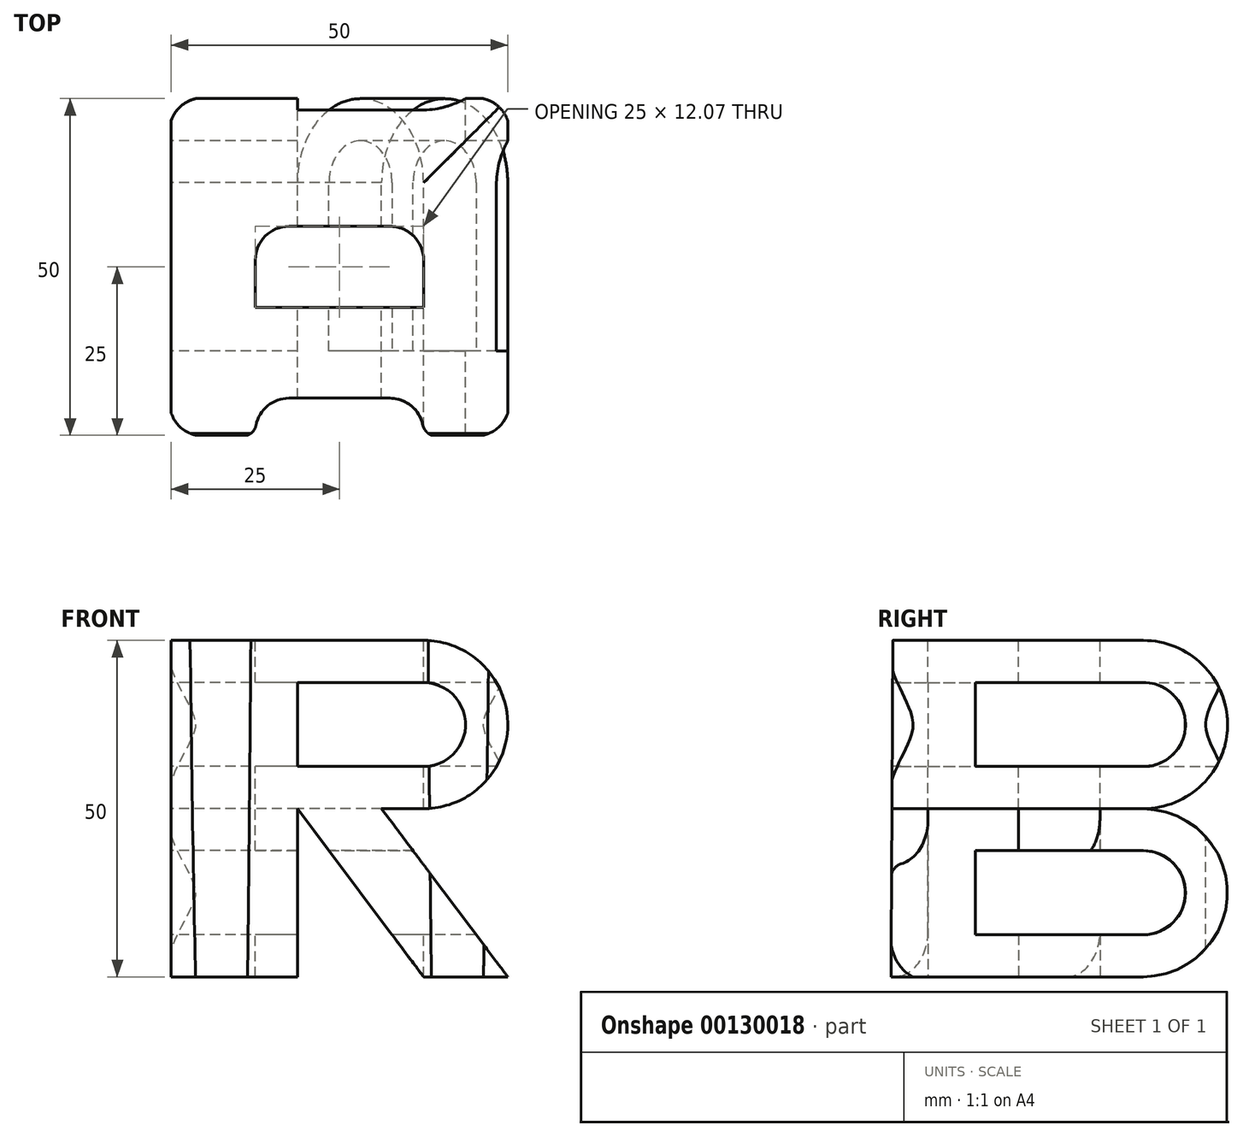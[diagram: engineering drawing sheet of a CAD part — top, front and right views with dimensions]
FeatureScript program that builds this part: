
annotation { "Feature Type Name" : "Feature", "Feature Type Description" : "" }
export const myFeature = defineFeature(function(context is Context, id is Id, definition is map)
    precondition{}
    {
        {
            var Q0;
            Q0=qCreatedBy(makeId("Front.planeOp"),FACE);
            var sketch = newSketch(context, id + "F0", { "sketchPlane" : qUnion([Q0])});
            skLineSegment(sketch, "E0.bottom", {"start": v(25, 25) * mm, "end": v(-25, 25) * mm, "construction": true});
            skLineSegment(sketch, "E0.top", {"start": v(25, -25) * mm, "end": v(-25, -25) * mm, "construction": true});
            skLineSegment(sketch, "E0.left", {"start": v(25, 25) * mm, "end": v(25, -25) * mm, "construction": true});
            skLineSegment(sketch, "E0.right", {"start": v(-25, 25) * mm, "end": v(-25, -25) * mm, "construction": true});
            skPoint(sketch, "E0.middle", {"position": v(0, 0) * mm});
            skLineSegment(sketch, "E1", {"start": v(0, 25) * mm, "end": v(0, -25) * mm, "construction": true});
            skLineSegment(sketch, "E2", {"start": v(25, 0) * mm, "end": v(-25, 0) * mm, "construction": true});
            skLineSegment(sketch, "E3", {"start": v(-25, 18.75) * mm, "end": v(25, 18.75) * mm, "construction": true});
            skLineSegment(sketch, "E4", {"start": v(-25, 12.5) * mm, "end": v(25, 12.5) * mm, "construction": true});
            skLineSegment(sketch, "E5", {"start": v(25, 12.5) * mm, "end": v(24.97, 10.97) * mm, "construction": true});
            skLineSegment(sketch, "E6", {"start": v(-25.04, 6.25) * mm, "end": v(25, 6.25) * mm, "construction": true});
            skLineSegment(sketch, "E7", {"start": v(-25, -6.25) * mm, "end": v(25, -6.25) * mm, "construction": true});
            skLineSegment(sketch, "E8", {"start": v(-25, -12.5) * mm, "end": v(25, -12.5) * mm, "construction": true});
            skLineSegment(sketch, "E9", {"start": v(-25, -18.75) * mm, "end": v(25, -18.75) * mm, "construction": true});
            skLineSegment(sketch, "E10", {"start": v(18.75, -25) * mm, "end": v(18.75, 25) * mm, "construction": true});
            skLineSegment(sketch, "E11", {"start": v(6.25, 25) * mm, "end": v(6.25, -25) * mm, "construction": true});
            skLineSegment(sketch, "E12", {"start": v(12.5, -25) * mm, "end": v(12.5, 25) * mm, "construction": true});
            skLineSegment(sketch, "E13", {"start": v(-6.25, 25) * mm, "end": v(-6.25, -25) * mm, "construction": true});
            skLineSegment(sketch, "E14", {"start": v(-12.5, -24.97) * mm, "end": v(-12.5, 25) * mm, "construction": true});
            skLineSegment(sketch, "E15", {"start": v(-18.75, 24.74) * mm, "end": v(-18.75, -25) * mm, "construction": true});
            skLineSegment(sketch, "E16", {"start": v(-25, -25) * mm, "end": v(-6.25, -25) * mm});
            skLineSegment(sketch, "E17", {"start": v(-6.25, -25) * mm, "end": v(-6.25, 0) * mm});
            skLineSegment(sketch, "E18", {"start": v(-25, -25) * mm, "end": v(-25, 25) * mm});
            skLineSegment(sketch, "E19", {"start": v(-25, 25) * mm, "end": v(12.5, 25) * mm});
            skArc(sketch, "E20", {"start": v(12.5, 0) * mm, "mid": v(25, 12.5) * mm, "end": v(12.5, 25) * mm});
            skLineSegment(sketch, "E21", {"start": v(6.25, 0) * mm, "end": v(12.5, 0) * mm});
            skLineSegment(sketch, "E22", {"start": v(-6.25, 6.25) * mm, "end": v(-6.25, 18.75) * mm});
            skLineSegment(sketch, "E23", {"start": v(-6.25, 18.75) * mm, "end": v(12.5, 18.75) * mm});
            skLineSegment(sketch, "E24", {"start": v(-6.25, 6.25) * mm, "end": v(12.5, 6.25) * mm});
            skArc(sketch, "E25", {"start": v(12.5, 6.25) * mm, "mid": v(18.75, 12.5) * mm, "end": v(12.5, 18.75) * mm});
            skLineSegment(sketch, "E26", {"start": v(-6.25, 0) * mm, "end": v(12.5, -25) * mm});
            skLineSegment(sketch, "E27", {"start": v(12.5, -25) * mm, "end": v(25, -25) * mm});
            skLineSegment(sketch, "E28", {"start": v(6.25, 0) * mm, "end": v(25, -25) * mm});
            skSolve(sketch);
        }
        {
            var Q0;
            Q0=qCreatedBy(makeId("Right.planeOp"),FACE);
            var sketch = newSketch(context, id + "F1", { "sketchPlane" : qUnion([Q0])});
            skLineSegment(sketch, "E29.bottom", {"start": v(25, 25) * mm, "end": v(-25, 25) * mm, "construction": true});
            skLineSegment(sketch, "E29.top", {"start": v(25, -25) * mm, "end": v(-25, -25) * mm, "construction": true});
            skLineSegment(sketch, "E29.left", {"start": v(25, 25) * mm, "end": v(25, -25) * mm, "construction": true});
            skLineSegment(sketch, "E29.right", {"start": v(-25, 25) * mm, "end": v(-25, -25) * mm, "construction": true});
            skPoint(sketch, "E29.middle", {"position": v(0, 0) * mm});
            skLineSegment(sketch, "E30", {"start": v(-25, 0) * mm, "end": v(25, 0) * mm, "construction": true});
            skLineSegment(sketch, "E31", {"start": v(0, 25) * mm, "end": v(0, -25) * mm, "construction": true});
            skLineSegment(sketch, "E32", {"start": v(-25, -18.75) * mm, "end": v(25, -18.75) * mm, "construction": true});
            skLineSegment(sketch, "E33", {"start": v(25, -12.5) * mm, "end": v(-25, -12.5) * mm, "construction": true});
            skLineSegment(sketch, "E34", {"start": v(-25, -6.25) * mm, "end": v(25, -6.25) * mm, "construction": true});
            skLineSegment(sketch, "E35", {"start": v(25, 6.25) * mm, "end": v(-25, 6.25) * mm, "construction": true});
            skLineSegment(sketch, "E36", {"start": v(-24.78, 12.5) * mm, "end": v(25, 12.5) * mm, "construction": true});
            skLineSegment(sketch, "E37", {"start": v(24.7, 18.75) * mm, "end": v(-25, 18.75) * mm, "construction": true});
            skLineSegment(sketch, "E38", {"start": v(-18.75, 25) * mm, "end": v(-18.75, -25) * mm, "construction": true});
            skLineSegment(sketch, "E39", {"start": v(-12.5, 25) * mm, "end": v(-12.5, -25) * mm, "construction": true});
            skLineSegment(sketch, "E40", {"start": v(-6.25, 25) * mm, "end": v(-6.25, -25) * mm, "construction": true});
            skLineSegment(sketch, "E41", {"start": v(6.25, 25) * mm, "end": v(6.25, -25) * mm, "construction": true});
            skLineSegment(sketch, "E42", {"start": v(12.5, -25) * mm, "end": v(12.5, 25) * mm, "construction": true});
            skLineSegment(sketch, "E43", {"start": v(18.75, 25) * mm, "end": v(18.75, -25) * mm, "construction": true});
            skLineSegment(sketch, "E44", {"start": v(-25, 25) * mm, "end": v(-25, -25) * mm});
            skLineSegment(sketch, "E45", {"start": v(12.5, -25) * mm, "end": v(-25, -25) * mm});
            skLineSegment(sketch, "E46", {"start": v(-24.74, 25.04) * mm, "end": v(12.5, 25) * mm});
            skLineSegment(sketch, "E47", {"start": v(12.5, 18.75) * mm, "end": v(-12.5, 18.75) * mm});
            skLineSegment(sketch, "E48", {"start": v(-12.5, 18.75) * mm, "end": v(-12.5, 6.25) * mm});
            skLineSegment(sketch, "E49", {"start": v(-12.5, 6.25) * mm, "end": v(12.5, 6.25) * mm});
            skLineSegment(sketch, "E50", {"start": v(12.5, -6.25) * mm, "end": v(-12.5, -6.25) * mm});
            skLineSegment(sketch, "E51", {"start": v(-12.5, -6.25) * mm, "end": v(-12.5, -18.75) * mm});
            skLineSegment(sketch, "E52", {"start": v(-12.5, -18.75) * mm, "end": v(12.5, -18.75) * mm});
            skArc(sketch, "E53", {"start": v(12.5, 0) * mm, "mid": v(25, 12.5) * mm, "end": v(12.5, 25) * mm});
            skArc(sketch, "E54", {"start": v(12.5, -25) * mm, "mid": v(25, -12.5) * mm, "end": v(12.5, 0) * mm});
            skLineSegment(sketch, "E55", {"start": v(-25, -25) * mm, "end": v(12.5, -25) * mm});
            skArc(sketch, "E56", {"start": v(12.5, 6.25) * mm, "mid": v(18.75, 12.5) * mm, "end": v(12.5, 18.75) * mm});
            skArc(sketch, "E57", {"start": v(12.5, -18.75) * mm, "mid": v(18.75, -12.5) * mm, "end": v(12.5, -6.25) * mm});
            skLineSegment(sketch, "E58", {"start": v(-24.74, 25.04) * mm, "end": v(-25, -25) * mm});
            skSolve(sketch);
        }
        {
            var Q0;
            Q0 = qSketchRegion(id + "F0", true);
            extrude(context, id + "F2", {"entities" : qUnion([Q0]), "endBound" : BoundingType.SYMMETRIC, "depth" : 50 * mm});
        }
        {
            var Q0;
            Q0 = qSketchRegion(id + "F1", true);
            extrude(context, id + "F3", {"entities" : qUnion([Q0]), "operationType" : NewBodyOperationType.INTERSECT, "endBound" : BoundingType.SYMMETRIC, "depth" : 50 * mm});
        }
        {
            var Q0;
            Q0=makeQuery(id+"F2.opExtrude","SWEPT_FACE",FACE,{"disambiguationData":[OSD([sQuery(id+"F0.wireOp",EDGE,"E19")])]});
            var sketch = newSketch(context, id + "F4", { "sketchPlane" : qUnion([Q0])});
            skLineSegment(sketch, "E59.bottom", {"start": v(20.27, 25.13) * mm, "end": v(-20.27, 25.13) * mm});
            skLineSegment(sketch, "E59.top", {"start": v(20.27, -25.13) * mm, "end": v(14.36, -25.13) * mm});
            skLineSegment(sketch, "E59.left", {"start": v(25.27, 20.13) * mm, "end": v(25.27, -20.13) * mm});
            skLineSegment(sketch, "E59.right", {"start": v(-25.27, 20.13) * mm, "end": v(-25.27, -20.13) * mm});
            skPoint(sketch, "E59.middle", {"position": v(0, 0) * mm});
            skLineSegment(sketch, "E60.left", {"start": v(8.42, -24.51) * mm, "end": v(8.42, -25.13) * mm});
            skLineSegment(sketch, "E60.right", {"start": v(-8.42, -24.51) * mm, "end": v(-8.42, -25.13) * mm});
            skPoint(sketch, "E60.middle", {"position": v(0, -25.13) * mm});
            skLineSegment(sketch, "E61.trimOffspring", {"start": v(-14.36, -25.13) * mm, "end": v(-20.27, -25.13) * mm});
            skPoint(sketch, "E62.visualSharp", {"position": v(25.27, 25.13) * mm});
            skArc(sketch, "E62.filletArc", {"start": v(25.27, 20.13) * mm, "mid": v(23.8, 23.66) * mm, "end": v(20.27, 25.13) * mm});
            skPoint(sketch, "E63.visualSharp", {"position": v(25.27, -25.13) * mm});
            skArc(sketch, "E63.filletArc", {"start": v(20.27, -25.13) * mm, "mid": v(23.8, -23.66) * mm, "end": v(25.27, -20.13) * mm});
            skPoint(sketch, "E64.visualSharp", {"position": v(-25.27, -25.13) * mm});
            skArc(sketch, "E64.filletArc", {"start": v(-25.27, -20.13) * mm, "mid": v(-23.8, -23.66) * mm, "end": v(-20.27, -25.13) * mm});
            skPoint(sketch, "E65.visualSharp", {"position": v(-25.27, 25.13) * mm});
            skArc(sketch, "E65.filletArc", {"start": v(-20.27, 25.13) * mm, "mid": v(-23.8, 23.66) * mm, "end": v(-25.27, 20.13) * mm});
            skPoint(sketch, "E66.visualSharp", {"position": v(-8.42, -19.51) * mm});
            skPoint(sketch, "E67.visualSharp", {"position": v(8.42, -19.51) * mm});
            skLineSegment(sketch, "E68.bottom", {"start": v(7.5, 6.04) * mm, "end": v(-7.5, 6.04) * mm});
            skLineSegment(sketch, "E68.top", {"start": v(12.5, -6.04) * mm, "end": v(-12.5, -6.04) * mm});
            skLineSegment(sketch, "E68.left", {"start": v(12.5, 1.04) * mm, "end": v(12.5, -6.04) * mm});
            skLineSegment(sketch, "E68.right", {"start": v(-12.5, 1.04) * mm, "end": v(-12.5, -6.04) * mm});
            skPoint(sketch, "E69.visualSharp", {"position": v(-12.5, 6.04) * mm});
            skArc(sketch, "E69.filletArc", {"start": v(-7.5, 6.04) * mm, "mid": v(-11.04, 4.57) * mm, "end": v(-12.5, 1.04) * mm});
            skPoint(sketch, "E70.visualSharp", {"position": v(12.5, 6.04) * mm});
            skArc(sketch, "E70.filletArc", {"start": v(12.5, 1.04) * mm, "mid": v(11.04, 4.57) * mm, "end": v(7.5, 6.04) * mm});
            skLineSegment(sketch, "E71.bottom", {"start": v(7.5, -19.51) * mm, "end": v(-7.5, -19.51) * mm});
            skLineSegment(sketch, "E71.left", {"start": v(12.5, -24.51) * mm, "end": v(12.5, -25.13) * mm});
            skLineSegment(sketch, "E71.right", {"start": v(-12.5, -24.51) * mm, "end": v(-12.5, -25.13) * mm});
            skPoint(sketch, "E72.orphan", {"position": v(12.5, -30.74) * mm});
            skPoint(sketch, "E73.orphan", {"position": v(-12.5, -30.74) * mm});
            skPoint(sketch, "E74.visualSharp", {"position": v(-12.5, -19.51) * mm});
            skArc(sketch, "E74.filletArc", {"start": v(-7.5, -19.51) * mm, "mid": v(-10.67, -20.64) * mm, "end": v(-12.4, -23.52) * mm});
            skPoint(sketch, "E75.visualSharp", {"position": v(12.5, -19.51) * mm});
            skArc(sketch, "E75.filletArc", {"start": v(12.4, -23.52) * mm, "mid": v(10.67, -20.64) * mm, "end": v(7.5, -19.51) * mm});
            skArc(sketch, "E76.filletArc", {"start": v(-14.36, -25.13) * mm, "mid": v(-13.1, -24.67) * mm, "end": v(-12.4, -23.52) * mm});
            skArc(sketch, "E77.filletArc", {"start": v(12.4, -23.52) * mm, "mid": v(13.1, -24.67) * mm, "end": v(14.36, -25.13) * mm});
            skSolve(sketch);
        }
        {
            var Q0;
            Q0 = qSketchRegion(id + "F4", true);
            extrude(context, id + "F5", {"entities" : qUnion([Q0]), "operationType" : NewBodyOperationType.INTERSECT, "oppositeDirection" : true, "depth" : 50 * mm});
        }
    });
